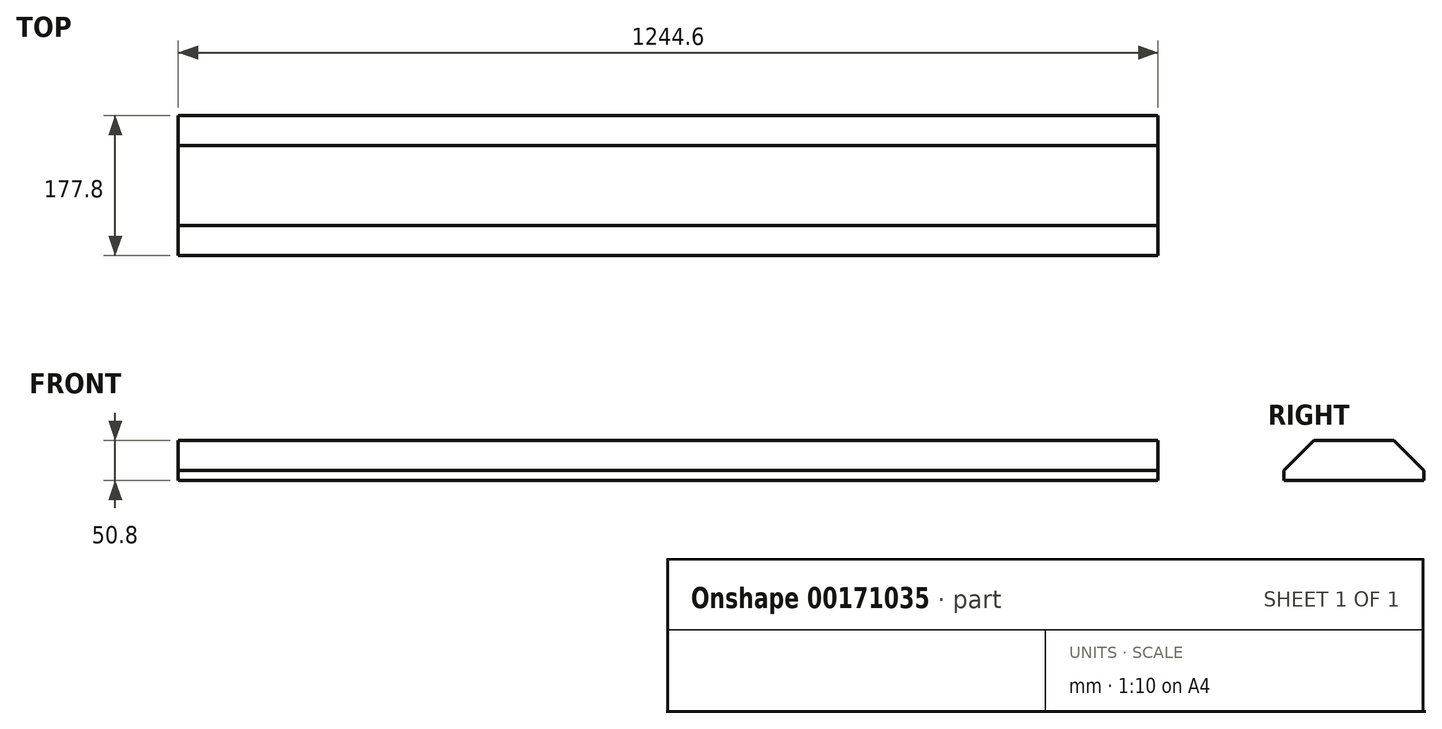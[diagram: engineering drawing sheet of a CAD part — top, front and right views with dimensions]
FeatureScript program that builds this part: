
annotation { "Feature Type Name" : "Feature", "Feature Type Description" : "" }
export const myFeature = defineFeature(function(context is Context, id is Id, definition is map)
    precondition{}
    {
        {
            var Q0;
            Q0=qCreatedBy(makeId("Top.planeOp"),FACE);
            var sketch = newSketch(context, id + "F0", { "sketchPlane" : qUnion([Q0])});
            skLineSegment(sketch, "E0.bottom", {"start": v(0, 0) * mm, "end": v(1244.6, 0) * mm});
            skLineSegment(sketch, "E0.top", {"start": v(0, 177.8) * mm, "end": v(1244.6, 177.8) * mm});
            skLineSegment(sketch, "E0.left", {"start": v(0, 0) * mm, "end": v(0, 177.8) * mm});
            skLineSegment(sketch, "E0.right", {"start": v(1244.6, 0) * mm, "end": v(1244.6, 177.8) * mm});
            skSolve(sketch);
        }
        {
            var Q0;
            Q0 = qSketchRegion(id + "F0", true);
            extrude(context, id + "F1", {"entities" : qUnion([Q0]), "depth" : 50.8 * mm});
        }
        {
            var Q0;
            Q0=makeQuery(id+"F1.opExtrude","CAP_EDGE",EDGE,{"disambiguationData":[OSD([sQuery(id+"F0.wireOp",EDGE,"E0.bottom")])],"isStart":false});
            var Q1;
            Q1=makeQuery(id+"F1.opExtrude","CAP_EDGE",EDGE,{"disambiguationData":[OSD([sQuery(id+"F0.wireOp",EDGE,"E0.top")])],"isStart":false});
            chamfer(context, id + "F2", {"entities" : qUnion([Q0, Q1]), "chamferType" : ChamferType.OFFSET_ANGLE, "width" : 38.1 * mm, "oppositeDirection" : false, "angle" : 45 * degree, "tangentPropagation" : true});
        }
    });
